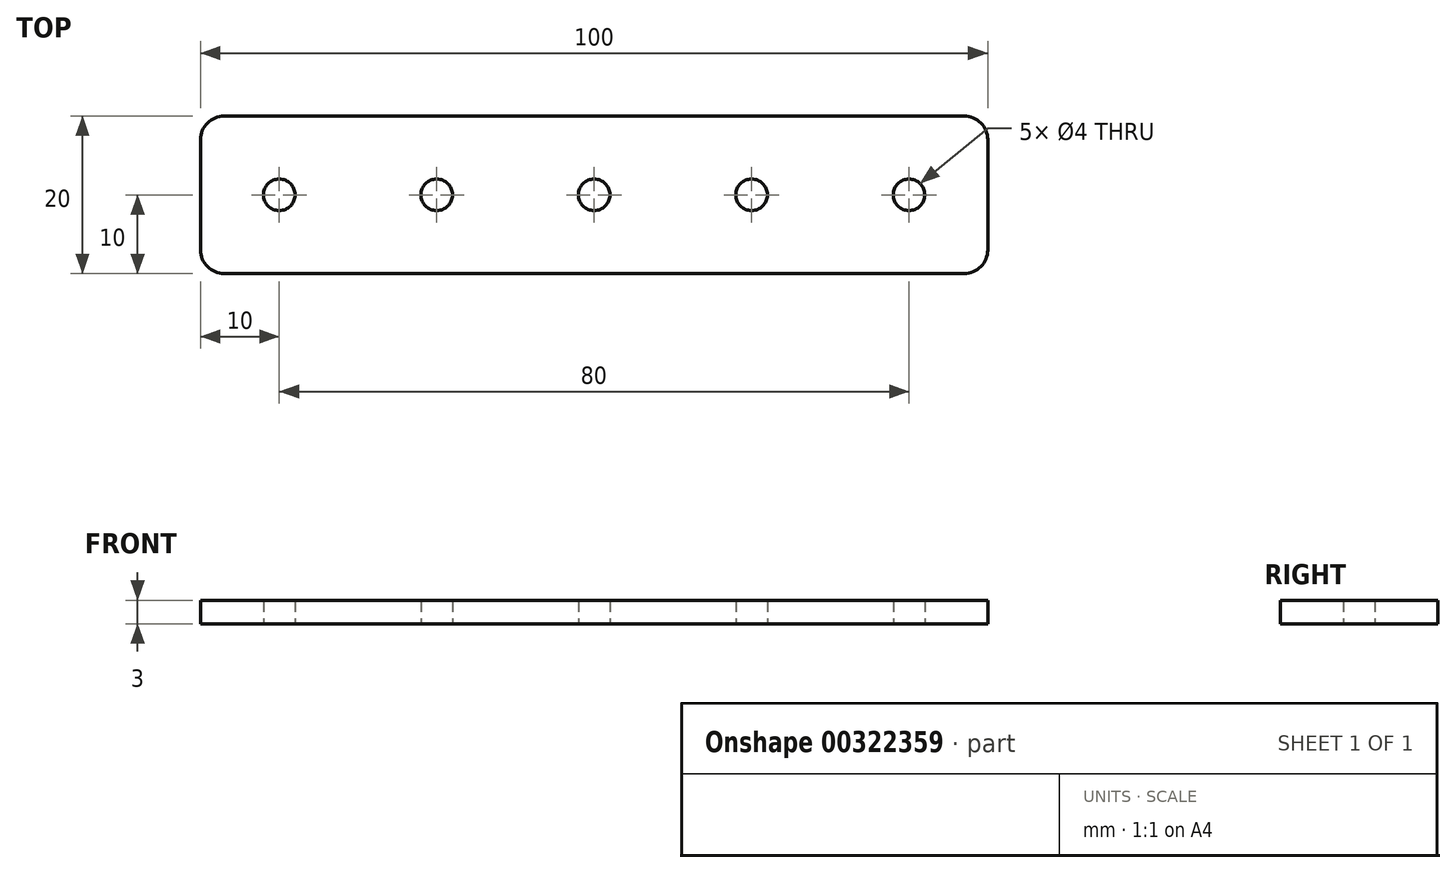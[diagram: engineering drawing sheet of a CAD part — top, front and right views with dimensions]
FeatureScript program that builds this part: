
annotation { "Feature Type Name" : "Feature", "Feature Type Description" : "" }
export const myFeature = defineFeature(function(context is Context, id is Id, definition is map)
    precondition{}
    {
        {
            var Q0;
            Q0=qCreatedBy(makeId("Top.planeOp"),FACE);
            var sketch = newSketch(context, id + "F0", { "sketchPlane" : qUnion([Q0])});
            skLineSegment(sketch, "E0.bottom", {"start": v(47, -10) * mm, "end": v(-47, -10) * mm});
            skLineSegment(sketch, "E0.top", {"start": v(47, 10) * mm, "end": v(-47, 10) * mm});
            skLineSegment(sketch, "E0.left", {"start": v(50, -7) * mm, "end": v(50, 7) * mm});
            skLineSegment(sketch, "E0.right", {"start": v(-50, -7) * mm, "end": v(-50, 7) * mm});
            skPoint(sketch, "E0.middle", {"position": v(0, 0) * mm});
            skCircle(sketch, "E1", {"center": v(-40, 0) * mm, "radius": 2 * mm});
            skCircle(sketch, "E2.1.0.0", {"center": v(-20, 0) * mm, "radius": 2 * mm});
            skCircle(sketch, "E2.2.0.0", {"center": v(0, 0) * mm, "radius": 2 * mm});
            skCircle(sketch, "E2.3.0.0", {"center": v(20, 0) * mm, "radius": 2 * mm});
            skLineSegment(sketch, "E2.direction1", {"start": v(-40, 0) * mm, "end": v(-20, 0) * mm, "construction": true});
            skCircle(sketch, "E3.0.4.0", {"center": v(40, 0) * mm, "radius": 2 * mm});
            skPoint(sketch, "E4.visualSharp", {"position": v(-50, 10) * mm});
            skArc(sketch, "E4.filletArc", {"start": v(-47, 10) * mm, "mid": v(-49.12, 9.12) * mm, "end": v(-50, 7) * mm});
            skPoint(sketch, "E5.visualSharp", {"position": v(-50, -10) * mm});
            skArc(sketch, "E5.filletArc", {"start": v(-50, -7) * mm, "mid": v(-49.12, -9.12) * mm, "end": v(-47, -10) * mm});
            skPoint(sketch, "E6.visualSharp", {"position": v(50, -10) * mm});
            skArc(sketch, "E6.filletArc", {"start": v(47, -10) * mm, "mid": v(49.12, -9.12) * mm, "end": v(50, -7) * mm});
            skPoint(sketch, "E7.visualSharp", {"position": v(50, 10) * mm});
            skArc(sketch, "E7.filletArc", {"start": v(50, 7) * mm, "mid": v(49.12, 9.12) * mm, "end": v(47, 10) * mm});
            skSolve(sketch);
        }
        {
            var Q0;
            Q0=qSketchRegion(id+"F0",true);
            extrude(context, id + "F1", {"entities" : qUnion([Q0]), "depth" : 3 * mm});
        }
    });
